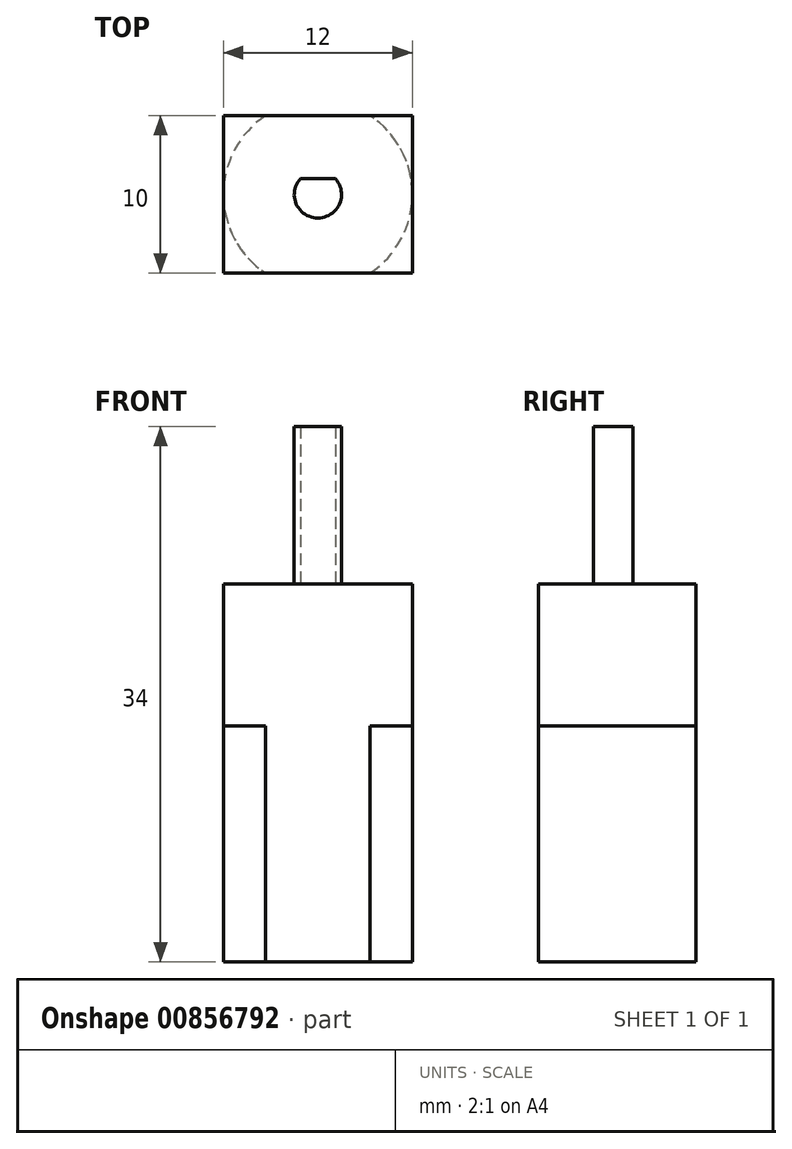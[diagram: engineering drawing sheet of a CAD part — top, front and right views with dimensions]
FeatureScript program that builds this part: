
annotation { "Feature Type Name" : "Feature", "Feature Type Description" : "" }
export const myFeature = defineFeature(function(context is Context, id is Id, definition is map)
    precondition{}
    {
        {
            var Q0;
            Q0=qCreatedBy(makeId("Top.planeOp"),FACE);
            var sketch = newSketch(context, id + "F0", { "sketchPlane" : qUnion([Q0])});
            skLineSegment(sketch, "E0", {"start": v(-3.32, 5) * mm, "end": v(3.32, 5) * mm});
            skLineSegment(sketch, "E1.MirrorCS", {"start": v(-3.32, -5) * mm, "end": v(3.32, -5) * mm});
            skArc(sketch, "E2", {"start": v(-3.32, 5) * mm, "mid": v(-6, 0) * mm, "end": v(-3.32, -5) * mm});
            skArc(sketch, "E3.MirrorCS", {"start": v(3.32, 5) * mm, "mid": v(6, 0) * mm, "end": v(3.32, -5) * mm});
            skSolve(sketch);
        }
        {
            var Q0;
            Q0=qSketchRegion(id+"F0",true);
            extrude(context, id + "F1", {"entities" : qUnion([Q0]), "depth" : 15 * mm, "offsetDistance" : 25 * mm});
        }
        {
            var Q0;
            Q0=makeQuery(id+"F1.opExtrude","CAP_FACE",FACE,{"disambiguationData":[OSD([sQuery(id+"F0.wireOp",EDGE,"E0"),sQuery(id+"F0.wireOp",EDGE,"E1.MirrorCS"),sQuery(id+"F0.wireOp",EDGE,"E2"),sQuery(id+"F0.wireOp",EDGE,"E3.MirrorCS")])],"isStart":false});
            var sketch = newSketch(context, id + "F2", { "sketchPlane" : qUnion([Q0])});
            skLineSegment(sketch, "E4", {"start": v(-6, 5) * mm, "end": v(6, 5) * mm});
            skPoint(sketch, "E4.startSnap0", {"position": v(-6, 0) * mm});
            skPoint(sketch, "E4.endSnap0", {"position": v(6, 0) * mm});
            skLineSegment(sketch, "E5", {"start": v(6, 5) * mm, "end": v(6, -5) * mm});
            skLineSegment(sketch, "E6", {"start": v(6, -5) * mm, "end": v(-6, -5) * mm});
            skLineSegment(sketch, "E7", {"start": v(-6, -5) * mm, "end": v(-6, 5) * mm});
            skSolve(sketch);
        }
        {
            var Q0;
            Q0=qSketchRegion(id+"F2",true);
            extrude(context, id + "F3", {"entities" : qUnion([Q0]), "operationType" : NewBodyOperationType.ADD, "depth" : 9 * mm, "offsetDistance" : 25 * mm});
        }
        {
            var Q0;
            Q0=makeQuery(id+"F3.opExtrude","CAP_FACE",FACE,{"disambiguationData":[OSD([sQuery(id+"F2.wireOp",EDGE,"E4"),sQuery(id+"F2.wireOp",EDGE,"E5"),sQuery(id+"F2.wireOp",EDGE,"E6"),sQuery(id+"F2.wireOp",EDGE,"E7")])],"isStart":false});
            var sketch = newSketch(context, id + "F4", { "sketchPlane" : qUnion([Q0])});
            skCircle(sketch, "E8", {"center": v(0, 0) * mm, "radius": 1.5 * mm});
            skLineSegment(sketch, "E9", {"start": v(-1.12, 1) * mm, "end": v(1.12, 1) * mm});
            skSolve(sketch);
        }
        {
            var Q0;
            {var subQ0=sQuery(id+"F4.wireOp",EDGE,"E9");Q0=makeQuery(id+"F4.imprint","IMPRINT",FACE,{"disambiguationData":[TD([[makeQuery(id+"F4.imprint","IMPRINT",EDGE,{"derivedFrom":subQ0}),-1.0]])]});}
            extrude(context, id + "F5", {"entities" : qUnion([Q0]), "operationType" : NewBodyOperationType.ADD, "depth" : 10 * mm, "offsetDistance" : 25 * mm});
        }
    });
